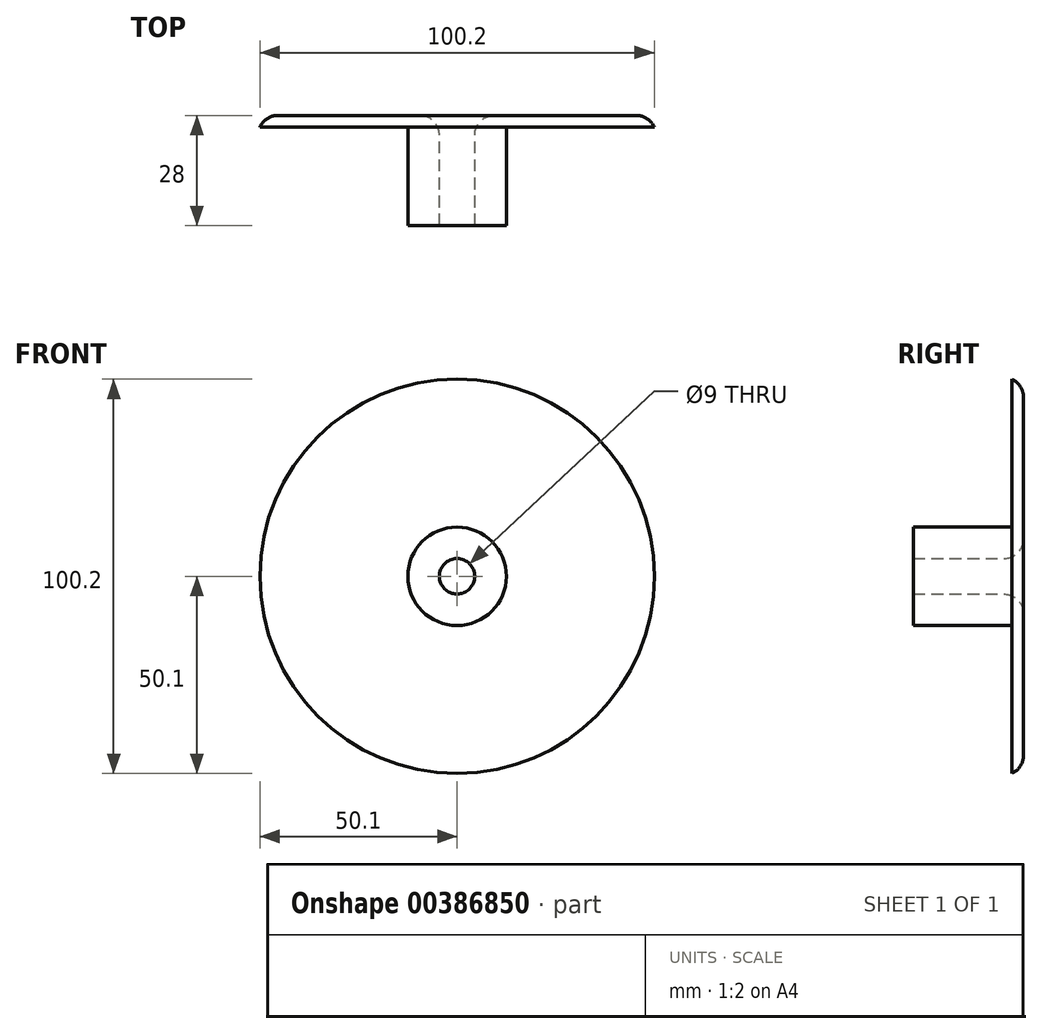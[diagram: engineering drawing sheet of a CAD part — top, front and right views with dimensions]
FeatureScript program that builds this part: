
annotation { "Feature Type Name" : "Feature", "Feature Type Description" : "" }
export const myFeature = defineFeature(function(context is Context, id is Id, definition is map)
    precondition{}
    {
        {
            var Q0;
            Q0=qCreatedBy(makeId("Front.planeOp"),FACE);
            var sketch = newSketch(context, id + "F0", { "sketchPlane" : qUnion([Q0])});
            skCircle(sketch, "E0", {"center": v(0, 0) * mm, "radius": 50.1 * mm});
            skCircle(sketch, "E1", {"center": v(0, 0) * mm, "radius": 4.5 * mm});
            skSolve(sketch);
        }
        {
            var Q0;
            Q0 = qSketchRegion(id + "F0", true);
            extrude(context, id + "F1", {"entities" : qUnion([Q0]), "depth" : 3 * mm});
        }
        {
            var Q0;
            Q0=makeQuery(id+"F1.opExtrude","CAP_FACE",FACE,{"disambiguationData":[OSD([sQuery(id+"F0.wireOp",EDGE,"E0"),sQuery(id+"F0.wireOp",EDGE,"E1")])],"isStart":false});
            var sketch = newSketch(context, id + "F2", { "sketchPlane" : qUnion([Q0])});
            skCircle(sketch, "E2", {"center": v(0, 0) * mm, "radius": 4.5 * mm});
            skCircle(sketch, "E3", {"center": v(0, 0) * mm, "radius": 12.5 * mm});
            skSolve(sketch);
        }
        {
            var Q0;
            Q0=makeQuery(id+"F2.imprint","IMPRINT",FACE,{"disambiguationData":[TD([[makeQuery(id+"F2.imprint","IMPRINT",EDGE,{"derivedFrom":sQuery(id+"F2.wireOp",EDGE,"E2")}),-1.0]])]});
            extrude(context, id + "F3", {"entities" : qUnion([Q0]), "operationType" : NewBodyOperationType.ADD, "depth" : 25 * mm});
        }
        {
            var Q0;
            Q0=makeQuery(id+"F1.opExtrude","CAP_FACE",FACE,{"disambiguationData":[OSD([sQuery(id+"F0.wireOp",EDGE,"E0"),sQuery(id+"F0.wireOp",EDGE,"E1")])],"isStart":true});
            fillet(context, id + "F4", {"entities" : qUnion([Q0]), "radius" : 5 * mm, "tangentPropagation" : true, "allowEdgeOverflow" : false});
        }
    });
